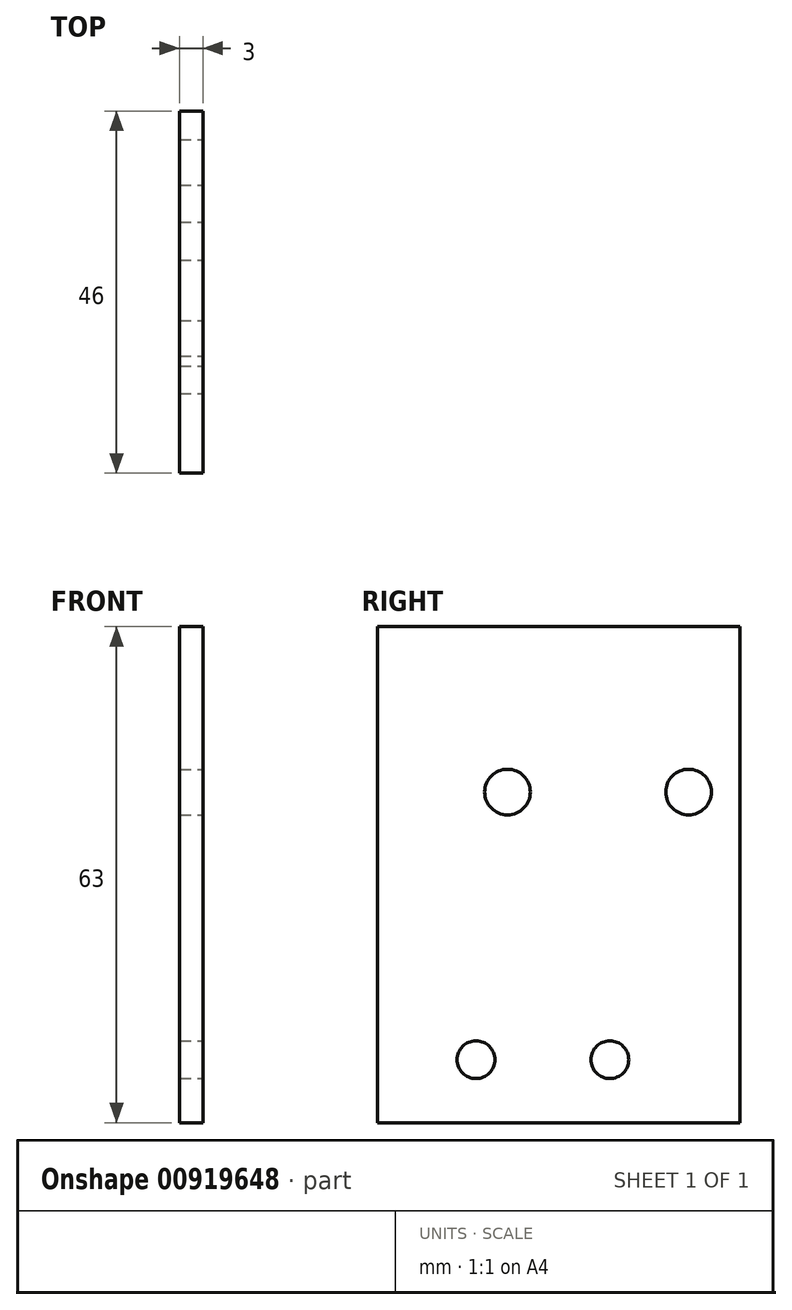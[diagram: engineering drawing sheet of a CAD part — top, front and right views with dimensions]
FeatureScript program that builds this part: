
annotation { "Feature Type Name" : "Feature", "Feature Type Description" : "" }
export const myFeature = defineFeature(function(context is Context, id is Id, definition is map)
    precondition{}
    {
        {
            var Q0;
            Q0=qCreatedBy(makeId("Right.planeOp"),FACE);
            var sketch = newSketch(context, id + "F0", { "sketchPlane" : qUnion([Q0])});
            skLineSegment(sketch, "E0.bottom", {"start": v(0, 0) * mm, "end": v(46, 0) * mm});
            skLineSegment(sketch, "E0.top", {"start": v(0, 63) * mm, "end": v(46, 63) * mm});
            skLineSegment(sketch, "E0.left", {"start": v(0, 0) * mm, "end": v(0, 63) * mm});
            skLineSegment(sketch, "E0.right", {"start": v(46, 0) * mm, "end": v(46, 63) * mm});
            skSolve(sketch);
        }
        {
            var Q0;
            Q0 = qSketchRegion(id + "F0", true);
            extrude(context, id + "F1", {"entities" : qUnion([Q0]), "depth" : 3 * mm, "offsetDistance" : 25 * mm});
        }
        {
            var Q0;
            Q0=makeQuery(id+"F1.opExtrude","CAP_FACE",FACE,{"disambiguationData":[OSD([sQuery(id+"F0.wireOp",EDGE,"E0.bottom"),sQuery(id+"F0.wireOp",EDGE,"E0.top"),sQuery(id+"F0.wireOp",EDGE,"E0.left"),sQuery(id+"F0.wireOp",EDGE,"E0.right")])],"isStart":false});
            var sketch = newSketch(context, id + "F2", { "sketchPlane" : qUnion([Q0])});
            skLineSegment(sketch, "E1.bottom", {"start": v(12.5, 8) * mm, "end": v(29.5, 8) * mm, "construction": true});
            skLineSegment(sketch, "E1.top", {"start": v(16.5, 42) * mm, "end": v(39.5, 42) * mm, "construction": true});
            skCircle(sketch, "E2", {"center": v(16.5, 42) * mm, "radius": 2.9 * mm});
            skCircle(sketch, "E3", {"center": v(39.5, 42) * mm, "radius": 2.9 * mm});
            skCircle(sketch, "E4", {"center": v(29.5, 8) * mm, "radius": 2.4 * mm});
            skCircle(sketch, "E5", {"center": v(12.5, 8) * mm, "radius": 2.4 * mm});
            skSolve(sketch);
        }
        {
            var Q0;
            Q0=makeQuery(id+"F2.imprint","IMPRINT",FACE,{"disambiguationData":[TD([[makeQuery(id+"F2.imprint","IMPRINT",EDGE,{"derivedFrom":sQuery(id+"F2.wireOp",EDGE,"E2")}),-1.0]])]});
            var Q1;
            Q1=sQuery(id+"F2.wireOp",EDGE,"E2");
            var Q2;
            Q2=sQuery(id+"F2.wireOp",EDGE,"E3");
            var Q3;
            Q3=sQuery(id+"F2.wireOp",EDGE,"E4");
            var Q4;
            Q4=sQuery(id+"F2.wireOp",EDGE,"E5");
            extrude(context, id + "F3", {"entities" : qUnion([Q0]), "operationType" : NewBodyOperationType.INTERSECT, "surfaceOperationType" : NewSurfaceOperationType.ADD, "surfaceEntities" : qUnion([Q1, Q2, Q3, Q4]), "endBound" : BoundingType.THROUGH_ALL, "oppositeDirection" : true, "depth" : 25 * mm, "offsetDistance" : 25 * mm});
        }
    });
